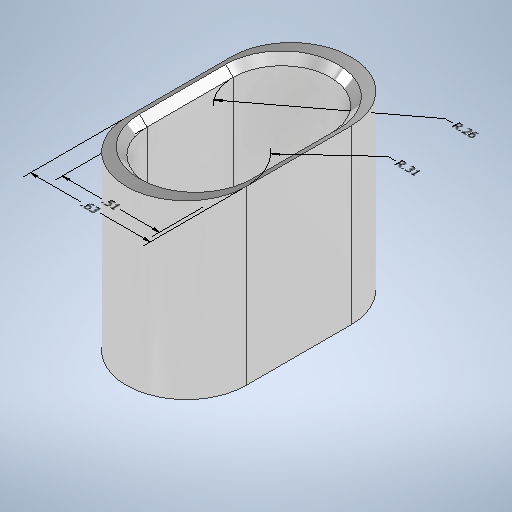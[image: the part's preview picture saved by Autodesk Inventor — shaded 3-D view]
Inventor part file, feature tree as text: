
AUTODESK INVENTOR PART (.ipt)
format: ipt  version: 2025.2 (Build 292293000, 293)  size: 273,408 bytes
history: native  units: in
note: dims shown in document units (in); Inventor stores cm internally (conversion verified against a paired STEP export)
features: other x5, extrude x3, sketch x3, chamfer x1
ambient origin geometry x8: Origin, YZ Plane, XZ Plane, XY Plane, X Axis, Y Axis, Z Axis, Center Point
bodies: Solid1 (feature_tree)
feature tree (12):
  other  "Annotations"
  extrude  "Extrusion1"  Depth=0.9055in TaperAngle=0.0deg
  extrude  "Extrusion2"  Depth=0.5118in
  extrude  "Extrusion3"  Depth=0.315in
  chamfer  "Chamfer1"  Distance=0.0984in
  sketch  "Sketch1"  dims[d4=0.6299in d5=1.1811in d6=0.9055in d7=0.0in]
  sketch  "Sketch4"  dims[d11=0.9646in d12=0.5118in]
  sketch  "Sketch5"  dims[d13=0.7087in d14=0.0in d15=0.2953in d16=0.0984in d17=0.7087in d18=0.0in d19=0.0394in d20=0.0787in d21=45.0deg d25=0.9824in d26=0.2559in d27=0.1239in d28=0.2482in d29=0.6299in d32=0.1875in d33=0.1817in d34=0.5118in d35=1.1341in d36=0.315in]
  other  "Radial Dimension 1"
  other  "Linear Dimension 2"
  other  "Linear Dimension 3"
  other  "Radial Dimension 2"
